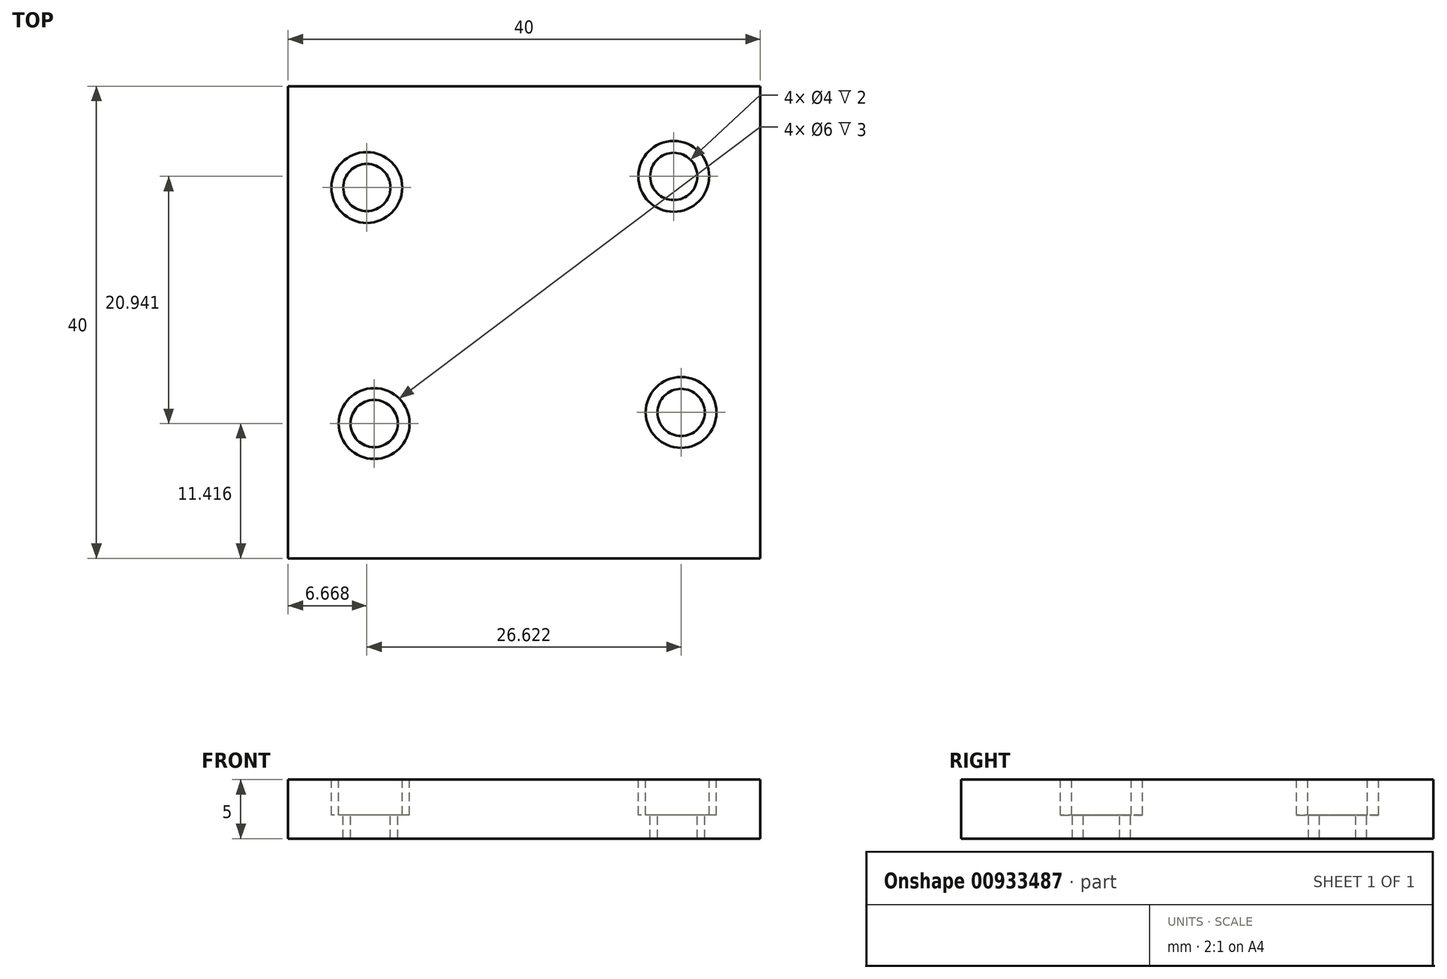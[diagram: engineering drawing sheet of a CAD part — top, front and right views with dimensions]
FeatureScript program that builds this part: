
annotation { "Feature Type Name" : "Feature", "Feature Type Description" : "" }
export const myFeature = defineFeature(function(context is Context, id is Id, definition is map)
    precondition{}
    {
        {
            var Q0;
            Q0=qCreatedBy(makeId("Top.planeOp"),FACE);
            var sketch = newSketch(context, id + "F0", { "sketchPlane" : qUnion([Q0])});
            skLineSegment(sketch, "E0.bottom", {"start": v(-20, 20) * mm, "end": v(20, 20) * mm});
            skLineSegment(sketch, "E0.top", {"start": v(-20, -20) * mm, "end": v(20, -20) * mm});
            skLineSegment(sketch, "E0.left", {"start": v(-20, 20) * mm, "end": v(-20, -20) * mm});
            skLineSegment(sketch, "E0.right", {"start": v(20, 20) * mm, "end": v(20, -20) * mm});
            skPoint(sketch, "E0.middle", {"position": v(0, 0) * mm});
            skSolve(sketch);
        }
        {
            var Q0;
            Q0 = qSketchRegion(id + "F0", true);
            extrude(context, id + "F1", {"entities" : qUnion([Q0]), "depth" : 5 * mm, "offsetDistance" : 25 * mm});
        }
        {
            var Q0;
            Q0=makeQuery(id+"F1.opExtrude","CAP_FACE",FACE,{"disambiguationData":[OSD([sQuery(id+"F0.wireOp",EDGE,"E0.bottom"),sQuery(id+"F0.wireOp",EDGE,"E0.top"),sQuery(id+"F0.wireOp",EDGE,"E0.left"),sQuery(id+"F0.wireOp",EDGE,"E0.right")])],"isStart":false});
            var sketch = newSketch(context, id + "F2", { "sketchPlane" : qUnion([Q0])});
            skCircle(sketch, "E1", {"center": v(-12.7, -8.58) * mm, "radius": 2 * mm});
            skCircle(sketch, "E2", {"center": v(-13.33, 11.42) * mm, "radius": 2 * mm});
            skCircle(sketch, "E3", {"center": v(12.67, 12.36) * mm, "radius": 2 * mm});
            skCircle(sketch, "E4", {"center": v(13.3, -7.64) * mm, "radius": 2 * mm});
            skSolve(sketch);
        }
        {
            var Q0;
            Q0 = qSketchRegion(id + "F2", true);
            extrude(context, id + "F3", {"entities" : qUnion([Q0]), "operationType" : NewBodyOperationType.REMOVE, "oppositeDirection" : true, "depth" : 5 * mm, "offsetDistance" : 25 * mm});
        }
        {
            var Q0;
            Q0=makeQuery(id+"F1.opExtrude","CAP_FACE",FACE,{"disambiguationData":[OSD([sQuery(id+"F0.wireOp",EDGE,"E0.bottom"),sQuery(id+"F0.wireOp",EDGE,"E0.top"),sQuery(id+"F0.wireOp",EDGE,"E0.left"),sQuery(id+"F0.wireOp",EDGE,"E0.right")])],"isStart":false});
            var sketch = newSketch(context, id + "F4", { "sketchPlane" : qUnion([Q0])});
            skCircle(sketch, "E5", {"center": v(-12.7, -8.58) * mm, "radius": 3 * mm});
            skCircle(sketch, "E6", {"center": v(-13.33, 11.42) * mm, "radius": 3 * mm});
            skCircle(sketch, "E7", {"center": v(12.67, 12.36) * mm, "radius": 3 * mm});
            skCircle(sketch, "E8", {"center": v(13.3, -7.64) * mm, "radius": 3 * mm});
            skSolve(sketch);
        }
        {
            var Q0;
            Q0 = qSketchRegion(id + "F4", true);
            extrude(context, id + "F5", {"entities" : qUnion([Q0]), "operationType" : NewBodyOperationType.REMOVE, "oppositeDirection" : true, "depth" : 3 * mm, "offsetDistance" : 25 * mm});
        }
    });
